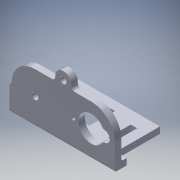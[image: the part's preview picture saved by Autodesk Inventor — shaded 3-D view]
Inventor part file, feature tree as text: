
AUTODESK INVENTOR PART (.ipt)
format: ipt  version: 2016 (Build 200138000, 138)  size: 236,032 bytes
history: native  units: in
note: dims shown in document units (in); Inventor stores cm internally (conversion verified against a paired STEP export)
features: extrude x7, sketch x6, fillet x3, direct_edit x3, move_body x3
ambient origin geometry x8: Origin, YZ Plane, XZ Plane, XY Plane, X Axis, Y Axis, Z Axis, Center Point
bodies: Solid1 (feature_tree)
feature tree (22):
  extrude  "Extrusion1"  Depth=0.1181in TaperAngle=0.0deg
  fillet  "Fillet1"  Radius=0.0591in
  fillet  "Fillet2"  Radius=0.0591in
  extrude  "Extrusion2"  Depth=1.0236in TaperAngle=0.0deg
  extrude  "Extrusion3"  Depth=0.0315in
  extrude  "Extrusion4"  Depth=0.515in
  fillet  "Fillet3"  Radius=1.172in
  extrude  "Extrusion5"  Depth=0.6413in TaperAngle=0.0deg
  direct_edit  "Direct Edit1"
  extrude  "Extrusion6"  Depth=0.4134in
  extrude  "Extrusion7"  Depth=0.2378in
  direct_edit  "Direct Edit2"
  direct_edit  "Direct Edit3"
  sketch  "Sketch1"  dims[d0=0.1181in d1=0.2953in d2=0.1181in d3=0.0in d4=0.0591in d5=0.0591in]
  sketch  "Sketch2"  dims[d11=0.9055in d12=0.0in d13=1.0236in d14=0.0in]
  sketch  "Sketch3"  dims[d17=1.0236in d18=0.0in d19=0.0315in]
  sketch  "Sketch5"  dims[d20=0.0669in d21=0.515in d22=1.172in]
  sketch  "Sketch6"  dims[d23=1.0236in d24=0.0in d25=0.0in d26=0.0in d27=0.6413in]
  sketch  "Sketch7"  dims[d28=0.1181in d29=0.4134in d30=0.2378in d31=0.3762in d32=0.0in d33=0.0in d34=0.1793in d35=0.3937in d36=0.0in d40=0.0in d41=0.0in d42=0.0394in d43=0.0in d44=0.0in d45=-0.0394in]
  move_body  "Move1"
  move_body  "Move2"
  move_body  "Move3"
